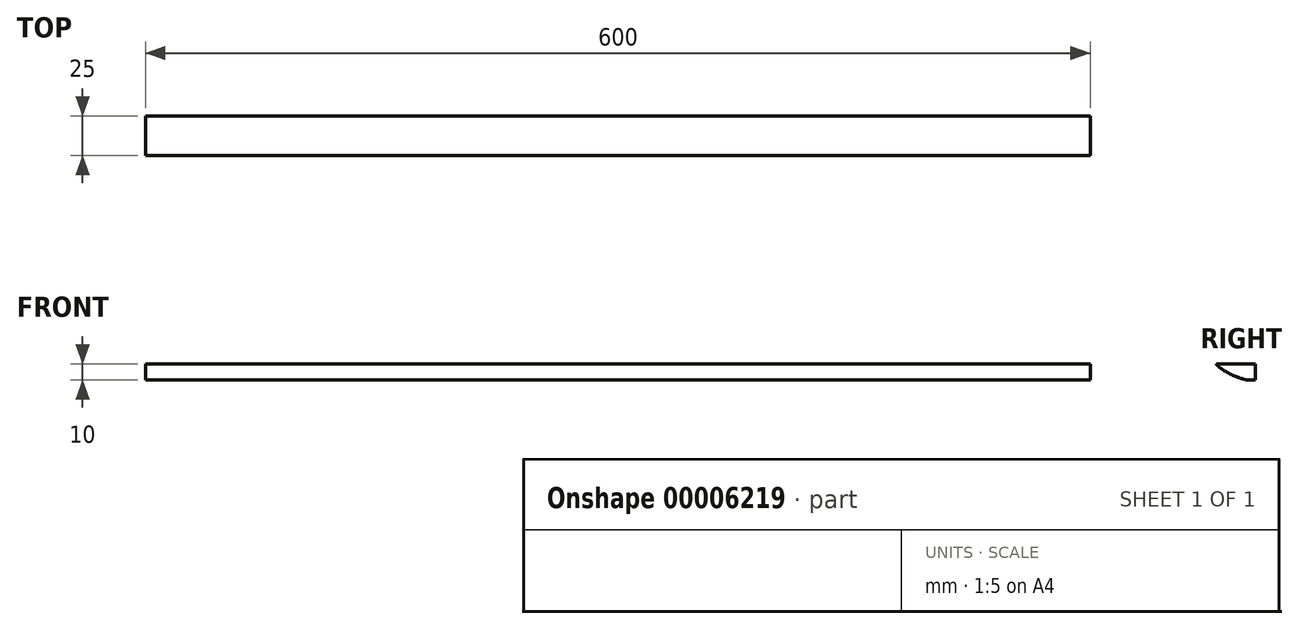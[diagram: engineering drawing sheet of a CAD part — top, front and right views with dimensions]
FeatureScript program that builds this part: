
annotation { "Feature Type Name" : "Feature", "Feature Type Description" : "" }
export const myFeature = defineFeature(function(context is Context, id is Id, definition is map)
    precondition{}
    {
        {
            var Q0;
            Q0=qCreatedBy(makeId("Front.planeOp"),FACE);
            var sketch = newSketch(context, id + "F0", { "sketchPlane" : qUnion([Q0])});
            skLineSegment(sketch, "E0.rect.bottom", {"start": v(300, 5) * mm, "end": v(-300, 5) * mm});
            skLineSegment(sketch, "E0.rect.top", {"start": v(300, -5) * mm, "end": v(-300, -5) * mm});
            skLineSegment(sketch, "E0.rect.left", {"start": v(300, 5) * mm, "end": v(300, -5) * mm});
            skLineSegment(sketch, "E0.rect.right", {"start": v(-300, 5) * mm, "end": v(-300, -5) * mm});
            skPoint(sketch, "E0.rect.middle", {"position": v(0, 0) * mm});
            skSolve(sketch);
        }
        {
            var Q0;
            Q0 = qSketchRegion(id + "F0", true);
            extrude(context, id + "F1", {"entities" : qUnion([Q0]), "depth" : 25 * mm});
        }
        {
            var Q0;
            Q0=makeQuery(id+"F1.opExtrude","CAP_EDGE",EDGE,{"disambiguationData":[OSD([sQuery(id+"F0.wireOp",EDGE,"E0.rect.top")])],"isStart":false});
            fillet(context, id + "F2", {"entities" : qUnion([Q0]), "radius" : 25 * mm, "tangentPropagation" : true, "rho" : 0.3, "crossSection" : FilletCrossSection.CONIC, "allowEdgeOverflow" : false});
        }
    });
